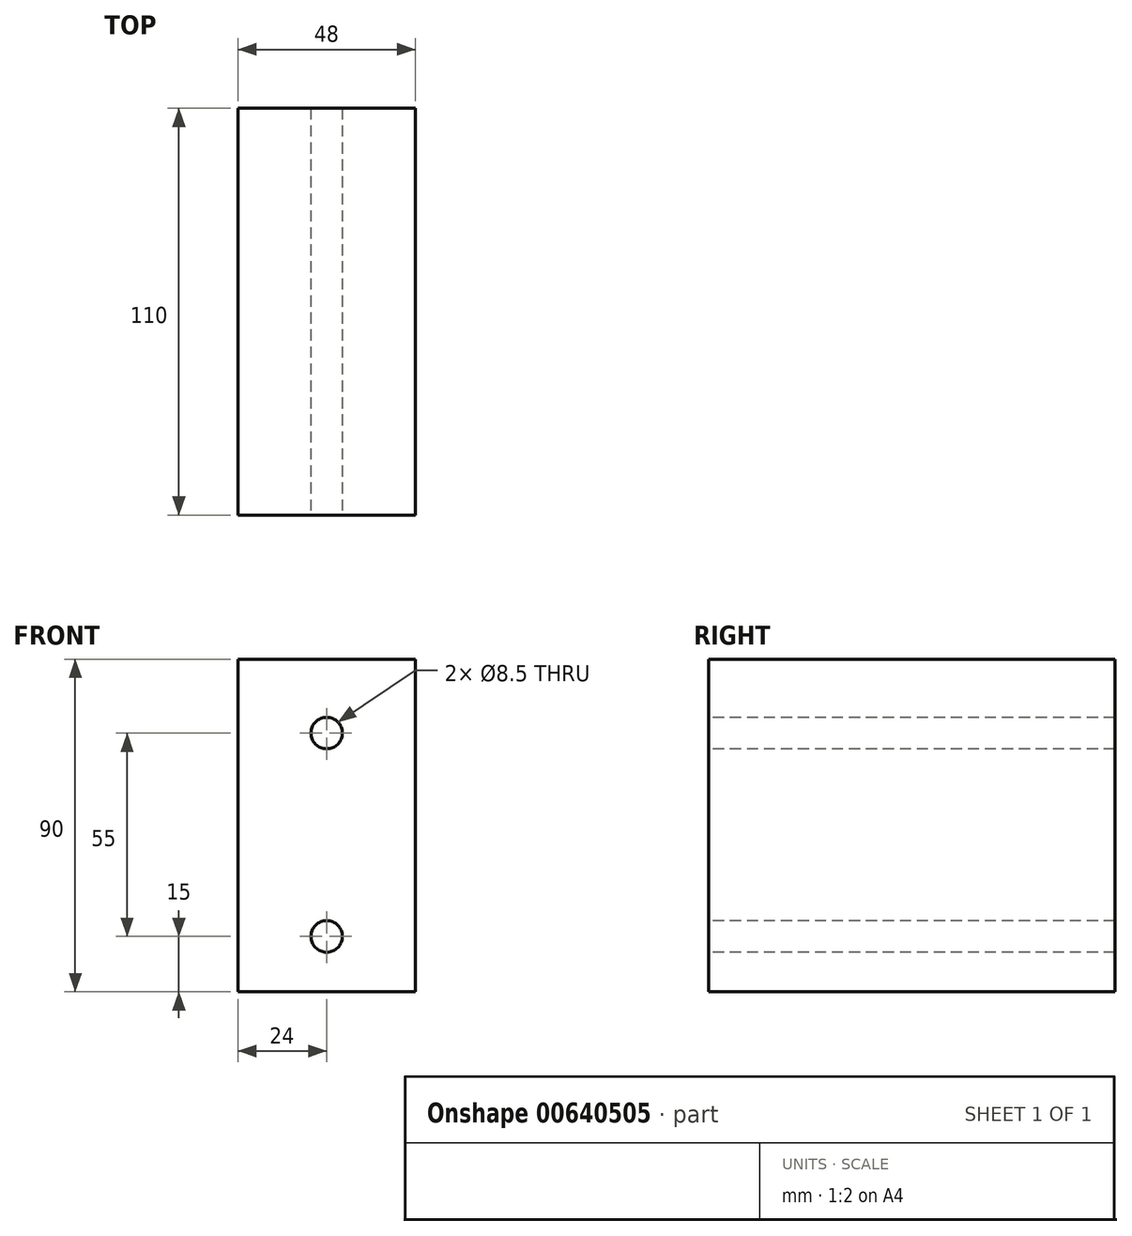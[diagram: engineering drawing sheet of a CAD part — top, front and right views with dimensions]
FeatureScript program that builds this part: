
annotation { "Feature Type Name" : "Feature", "Feature Type Description" : "" }
export const myFeature = defineFeature(function(context is Context, id is Id, definition is map)
    precondition{}
    {
        {
            var Q0;
            Q0=qCreatedBy(makeId("Front.planeOp"),FACE);
            var sketch = newSketch(context, id + "F0", { "sketchPlane" : qUnion([Q0])});
            skLineSegment(sketch, "E0.bottom", {"start": v(0, 0) * mm, "end": v(48, 0) * mm});
            skLineSegment(sketch, "E0.top", {"start": v(0, 90) * mm, "end": v(48, 90) * mm});
            skLineSegment(sketch, "E0.left", {"start": v(0, 0) * mm, "end": v(0, 90) * mm});
            skLineSegment(sketch, "E0.right", {"start": v(48, 0) * mm, "end": v(48, 90) * mm});
            skSolve(sketch);
        }
        {
            var Q0;
            Q0=makeQuery(id+"F0.imprint","IMPRINT",FACE,{"disambiguationData":[TD([[makeQuery(id+"F0.imprint","IMPRINT",EDGE,{"derivedFrom":sQuery(id+"F0.wireOp",EDGE,"E0.bottom")}),1.0]])]});
            extrude(context, id + "F1", {"entities" : qUnion([Q0]), "depth" : 110 * mm, "offsetDistance" : 25 * mm});
        }
        {
            var Q0;
            Q0=makeQuery(id+"F1.opExtrude","CAP_FACE",FACE,{"disambiguationData":[OSD([sQuery(id+"F0.wireOp",EDGE,"E0.bottom"),sQuery(id+"F0.wireOp",EDGE,"E0.top"),sQuery(id+"F0.wireOp",EDGE,"E0.left"),sQuery(id+"F0.wireOp",EDGE,"E0.right")])],"isStart":false});
            var sketch = newSketch(context, id + "F2", { "sketchPlane" : qUnion([Q0])});
            skPoint(sketch, "E1", {"position": v(24, 70) * mm});
            skPoint(sketch, "E1.positionSnap0", {"position": v(24, 90) * mm});
            skPoint(sketch, "E2", {"position": v(24, 15) * mm});
            skSolve(sketch);
        }
        {
            var Q0;
            Q0=sQuery(id+"F2.wireOp",VERTEX,"E1");
            var Q1;
            Q1=sQuery(id+"F2.wireOp",VERTEX,"E2");
            var Q2;
            Q2=makeQuery(id+"F1.opExtrude","SWEPT_BODY",BODY,{"disambiguationData":[OSD([sQuery(id+"F0.wireOp",EDGE,"E0.bottom"),sQuery(id+"F0.wireOp",EDGE,"E0.top"),sQuery(id+"F0.wireOp",EDGE,"E0.left"),sQuery(id+"F0.wireOp",EDGE,"E0.right")])]});
            hole(context, id + "F3", {"style" : HoleStyle.SIMPLE, "endStyle" : HoleEndStyle.THROUGH, "standardTappedOrClearance" : lookupTablePath({ "standard" : "ISO", "engagement" : "75%", "pitch" : "1.5 mm", "size" : "M10", "type" : "Tapped" }), "standardBlindInLast" : lookupTablePath({ "standard" : "ISO", "engagement" : "75%", "pitch" : "1.5 mm", "size" : "M10", "type" : "Tapped" }), "holeDiameter" : 8.5 * mm, "majorDiameter" : 10 * mm, "showTappedDepth" : true, "isTappedThrough" : true, "tappedDepth" : 14.5 * mm, "tapClearance" : 3, "startFromSketch" : true, "locations" : qUnion([Q0, Q1]), "scope" : qUnion([Q2])});
        }
        {
            var Q0;
            Q0=makeQuery(id+"F1.opExtrude","SWEPT_FACE",FACE,{"disambiguationData":[OSD([sQuery(id+"F0.wireOp",EDGE,"E0.bottom")])]});
            var sketch = newSketch(context, id + "F4", { "sketchPlane" : qUnion([Q0])});
            skPoint(sketch, "E3", {"position": v(24, 110) * mm});
            skPoint(sketch, "E4", {"position": v(24, 20) * mm});
            skSolve(sketch);
        }
        {
            var Q0;
            {var subQ0=sQuery(id+"F0.wireOp",EDGE,"E0.bottom");Q0=makeQuery(id+"F4.imprint","IMPRINT",FACE,{"disambiguationData":[TD([[makeQuery(id+"F4.imprint","IMPRINT",EDGE,{"derivedFrom":makeQuery(id+"F1.opExtrude","CAP_EDGE",EDGE,{"disambiguationData":[OSD([subQ0])],"isStart":true})}),1.0]])]});}
            var sketch = newSketch(context, id + "F5", { "sketchPlane" : qUnion([Q0])});
            skCircle(sketch, "E5", {"center": v(24, 20) * mm, "radius": 16 * mm});
            skSolve(sketch);
        }
        {
            var Q0;
            Q0=sQuery(id+"F5.wireOp",EDGE,"E5");
            extrude(context, id + "F6", {"bodyType" : ToolBodyType.SURFACE, "surfaceEntities" : qUnion([Q0]), "depth" : 13 * mm, "offsetDistance" : 25 * mm});
        }
    });
